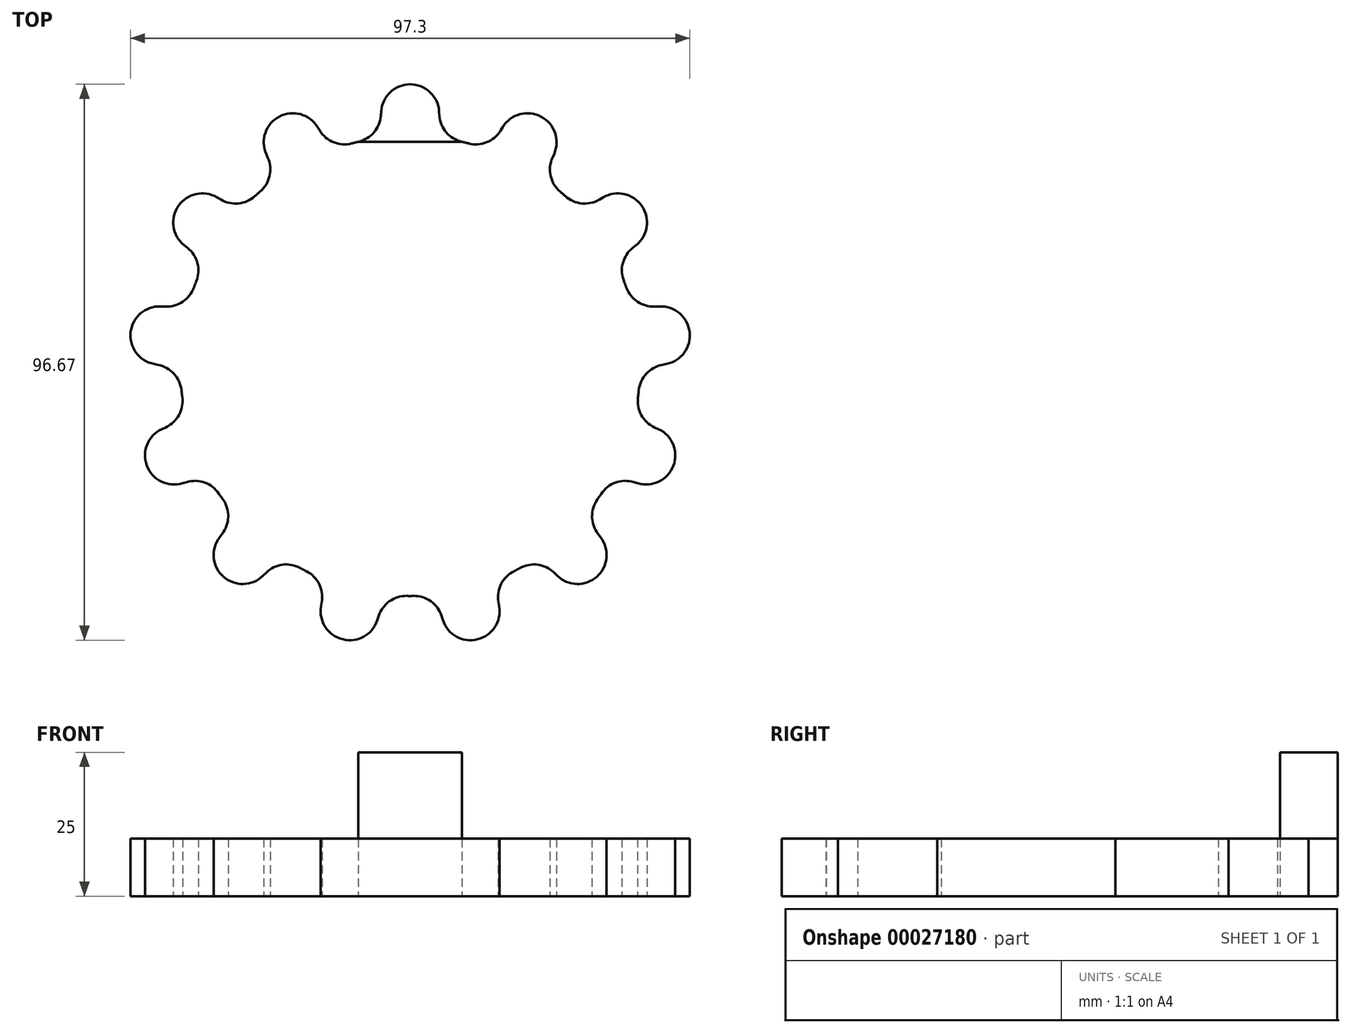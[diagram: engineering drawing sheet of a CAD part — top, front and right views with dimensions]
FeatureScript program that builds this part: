
annotation { "Feature Type Name" : "Feature", "Feature Type Description" : "" }
export const myFeature = defineFeature(function(context is Context, id is Id, definition is map)
    precondition{}
    {
        {
            var Q0;
            Q0=qCreatedBy(makeId("Top.planeOp"),FACE);
            var sketch = newSketch(context, id + "F0", { "sketchPlane" : qUnion([Q0])});
            skCircle(sketch, "E0", {"center": v(0, 0) * mm, "radius": 40 * mm});
            skSolve(sketch);
        }
        {
            var Q0;
            Q0=qCreatedBy(makeId("Top.planeOp"),FACE);
            var sketch = newSketch(context, id + "F1", { "sketchPlane" : qUnion([Q0])});
            skLineSegment(sketch, "E1", {"start": v(9, 38.97) * mm, "end": v(-9, 38.97) * mm});
            skLineSegment(sketch, "E2", {"start": v(0, 38.97) * mm, "end": v(0, 48.97) * mm, "construction": true});
            skPoint(sketch, "E3.visualSharp", {"position": v(0, 48.97) * mm});
            skArc(sketch, "E4", {"start": v(5.1, 43.53) * mm, "mid": v(6.3, 40.6) * mm, "end": v(9, 38.97) * mm});
            skLineSegment(sketch, "E5", {"start": v(5.1, 43.53) * mm, "end": v(5.04, 44.3) * mm});
            skArc(sketch, "E6", {"start": v(-9, 38.97) * mm, "mid": v(-6.3, 40.6) * mm, "end": v(-5.1, 43.53) * mm});
            skLineSegment(sketch, "E7", {"start": v(-5.1, 43.53) * mm, "end": v(-5.04, 44.3) * mm});
            skArc(sketch, "E8", {"start": v(5.04, 44.3) * mm, "mid": v(0, 48.97) * mm, "end": v(-5.04, 44.3) * mm});
            skSolve(sketch);
        }
        {
            var Q0;
            Q0=makeQuery(id+"F0.imprint","IMPRINT",FACE,{"disambiguationData":[TD([[makeQuery(id+"F0.imprint","IMPRINT",EDGE,{"derivedFrom":sQuery(id+"F0.wireOp",EDGE,"E0")}),1.0]])]});
            extrude(context, id + "F2", {"entities" : qUnion([Q0]), "depth" : 10 * mm});
        }
        {
            var Q0;
            Q0=makeQuery(id+"F1.imprint","IMPRINT",FACE,{"disambiguationData":[TD([[makeQuery(id+"F1.imprint","IMPRINT",EDGE,{"derivedFrom":sQuery(id+"F1.wireOp",EDGE,"E1")}),-1.0]])]});
            extrude(context, id + "F3", {"entities" : qUnion([Q0]), "depth" : 10 * mm});
        }
        {
            var Q0;
            Q0=qCreatedBy(makeId("Front.planeOp"),FACE);
            var sketch = newSketch(context, id + "F4", { "sketchPlane" : qUnion([Q0])});
            skLineSegment(sketch, "E9", {"start": v(0, 0) * mm, "end": v(0, 47.45) * mm, "construction": true});
            skSolve(sketch);
        }
        {
            var Q0;
            Q0=makeQuery(id+"F3.opExtrude","SWEPT_BODY",BODY,{"disambiguationData":[OSD([sQuery(id+"F1.wireOp",EDGE,"2741c680-6c6d-40f1-9316-29b68bc0c77f"),sQuery(id+"F1.wireOp",EDGE,"db7865a8-f3bb-47fc-98af-5aa2129b3a14"),sQuery(id+"F1.wireOp",EDGE,"E1"),sQuery(id+"F1.wireOp",EDGE,"E3.filletArc")])]});
            var Q1;
            Q1=sQuery(id+"F4.wireOp",EDGE,"E9");
            circularPattern(context, id + "F5", {"operationType" : NewBodyOperationType.ADD, "entities" : qUnion([Q0]), "axis" : qUnion([Q1]), "angle" : 360 * degree, "instanceCount" : 13, "equalSpace" : true, "computeTransformsWithoutBuiltin" : true});
        }
        {
            var Q0;
            Q0 = qSketchRegion(id + "F1", true);
            extrude(context, id + "F6", {"entities" : qUnion([Q0]), "depth" : 25 * mm});
        }
    });
